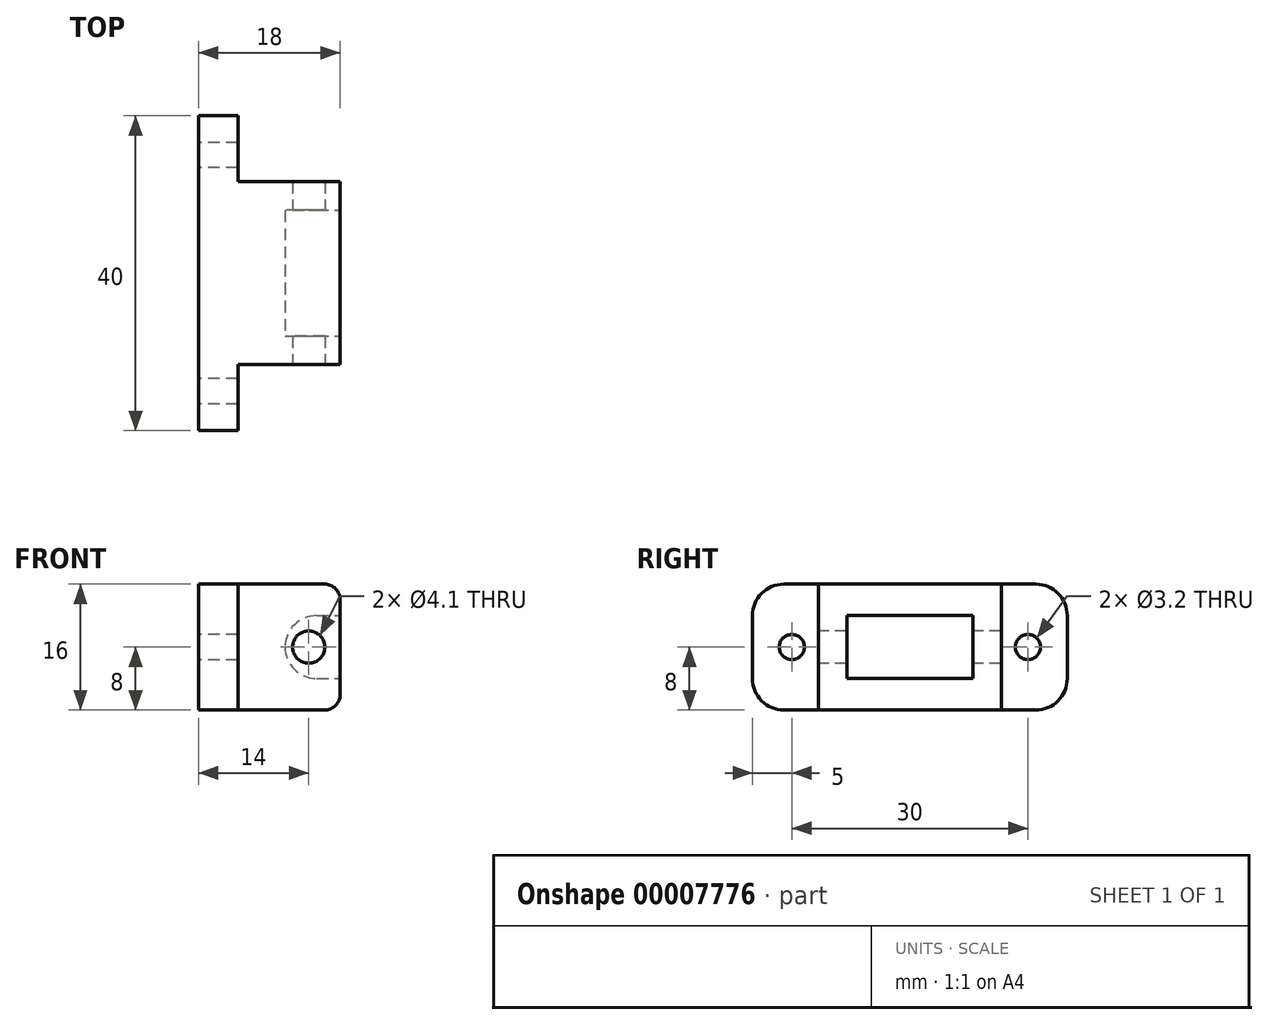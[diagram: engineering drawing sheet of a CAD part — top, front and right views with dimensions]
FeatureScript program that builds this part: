
annotation { "Feature Type Name" : "Feature", "Feature Type Description" : "" }
export const myFeature = defineFeature(function(context is Context, id is Id, definition is map)
    precondition{}
    {
        {
            var Q0;
            Q0=qCreatedBy(makeId("Right.planeOp"),FACE);
            var sketch = newSketch(context, id + "F0", { "sketchPlane" : qUnion([Q0])});
            skLineSegment(sketch, "E0.rect.bottom", {"start": v(16, 8) * mm, "end": v(-16, 8) * mm});
            skLineSegment(sketch, "E0.rect.top", {"start": v(16, -8) * mm, "end": v(-16, -8) * mm});
            skLineSegment(sketch, "E0.rect.left", {"start": v(20, 4) * mm, "end": v(20, -4) * mm});
            skLineSegment(sketch, "E0.rect.right", {"start": v(-20, 4) * mm, "end": v(-20, -4) * mm});
            skPoint(sketch, "E0.rect.middle", {"position": v(0, 0) * mm});
            skLineSegment(sketch, "E1", {"start": v(0, 11.54) * mm, "end": v(0, -21.77) * mm, "construction": true});
            skCircle(sketch, "E2", {"center": v(-15, 0) * mm, "radius": 1.6 * mm});
            skCircle(sketch, "E3.0.MirrorC", {"center": v(15, 0) * mm, "radius": 1.6 * mm});
            skPoint(sketch, "E4.visualSharp", {"position": v(-20, 8) * mm});
            skArc(sketch, "E4.filletArc", {"start": v(-16, 8) * mm, "mid": v(-18.83, 6.83) * mm, "end": v(-20, 4) * mm});
            skPoint(sketch, "E5.visualSharp", {"position": v(20, 8) * mm});
            skArc(sketch, "E5.filletArc", {"start": v(20, 4) * mm, "mid": v(18.83, 6.83) * mm, "end": v(16, 8) * mm});
            skPoint(sketch, "E6.visualSharp", {"position": v(20, -8) * mm});
            skArc(sketch, "E6.filletArc", {"start": v(16, -8) * mm, "mid": v(18.83, -6.83) * mm, "end": v(20, -4) * mm});
            skPoint(sketch, "E7.visualSharp", {"position": v(-20, -8) * mm});
            skArc(sketch, "E7.filletArc", {"start": v(-20, -4) * mm, "mid": v(-18.83, -6.83) * mm, "end": v(-16, -8) * mm});
            skSolve(sketch);
        }
        {
            var Q0;
            Q0 = qSketchRegion(id + "F0", true);
            extrude(context, id + "F1", {"entities" : qUnion([Q0]), "depth" : 10 * mm});
        }
        {
            var Q0;
            Q0=makeQuery(id+"F1.opExtrude","CAP_FACE",FACE,{"disambiguationData":[OSD([sQuery(id+"F0.wireOp",EDGE,"E0.rect.bottom"),sQuery(id+"F0.wireOp",EDGE,"E0.rect.top"),sQuery(id+"F0.wireOp",EDGE,"E0.rect.left"),sQuery(id+"F0.wireOp",EDGE,"E0.rect.right"),sQuery(id+"F0.wireOp",EDGE,"E2"),sQuery(id+"F0.wireOp",EDGE,"E3.0.MirrorC"),sQuery(id+"F0.wireOp",EDGE,"E4.filletArc"),sQuery(id+"F0.wireOp",EDGE,"E5.filletArc"),sQuery(id+"F0.wireOp",EDGE,"E6.filletArc"),sQuery(id+"F0.wireOp",EDGE,"E7.filletArc")])],"isStart":false});
            var sketch = newSketch(context, id + "F2", { "sketchPlane" : qUnion([Q0])});
            skLineSegment(sketch, "E8.rect.bottom", {"start": v(11.63, 8) * mm, "end": v(-11.63, 8) * mm});
            skLineSegment(sketch, "E8.rect.top", {"start": v(11.63, -8) * mm, "end": v(-11.63, -8) * mm});
            skLineSegment(sketch, "E8.rect.left", {"start": v(11.63, 8) * mm, "end": v(11.63, -8) * mm});
            skLineSegment(sketch, "E8.rect.right", {"start": v(-11.63, 8) * mm, "end": v(-11.63, -8) * mm});
            skPoint(sketch, "E8.rect.middle", {"position": v(0, 0) * mm});
            skSolve(sketch);
        }
        {
            var Q0;
            Q0 = qSketchRegion(id + "F2", true);
            extrude(context, id + "F3", {"entities" : qUnion([Q0]), "operationType" : NewBodyOperationType.ADD, "depth" : 8 * mm});
        }
        {
            var Q0;
            Q0=makeQuery(id+"F3.opExtrude","CAP_FACE",FACE,{"disambiguationData":[OSD([sQuery(id+"F2.wireOp",EDGE,"E8.rect.bottom"),sQuery(id+"F2.wireOp",EDGE,"E8.rect.top"),sQuery(id+"F2.wireOp",EDGE,"E8.rect.left"),sQuery(id+"F2.wireOp",EDGE,"E8.rect.right")])],"isStart":false});
            var sketch = newSketch(context, id + "F4", { "sketchPlane" : qUnion([Q0])});
            skLineSegment(sketch, "E9.rect.bottom", {"start": v(8, 4) * mm, "end": v(-8, 4) * mm});
            skLineSegment(sketch, "E9.rect.top", {"start": v(8, -4) * mm, "end": v(-8, -4) * mm});
            skLineSegment(sketch, "E9.rect.left", {"start": v(8, 4) * mm, "end": v(8, -4) * mm});
            skLineSegment(sketch, "E9.rect.right", {"start": v(-8, 4) * mm, "end": v(-8, -4) * mm});
            skPoint(sketch, "E9.rect.middle", {"position": v(0, 0) * mm});
            skSolve(sketch);
        }
        {
            var Q0;
            Q0 = qSketchRegion(id + "F4", true);
            extrude(context, id + "F5", {"entities" : qUnion([Q0]), "operationType" : NewBodyOperationType.REMOVE, "oppositeDirection" : true, "depth" : 7 * mm});
        }
        {
            var Q0;
            Q0=makeQuery(id+"F5.boolean.opBoolean","COPY",EDGE,{"derivedFrom":makeQuery(id+"F5.opExtrude","CAP_EDGE",EDGE,{"disambiguationData":[OSD([sQuery(id+"F4.wireOp",EDGE,"E9.rect.bottom")])],"isStart":false})});
            fillet(context, id + "F6", {"entities" : qUnion([Q0]), "radius" : 4 * mm, "tangentPropagation" : true, "allowEdgeOverflow" : false});
        }
        {
            var Q0;
            Q0=makeQuery(id+"F5.boolean.opBoolean","COPY",EDGE,{"derivedFrom":makeQuery(id+"F5.opExtrude","CAP_EDGE",EDGE,{"disambiguationData":[OSD([sQuery(id+"F4.wireOp",EDGE,"E9.rect.top")])],"isStart":false})});
            fillet(context, id + "F7", {"entities" : qUnion([Q0]), "radius" : 4 * mm, "tangentPropagation" : true, "allowEdgeOverflow" : false});
        }
        {
            var Q0;
            Q0=makeQuery(id+"F3.opExtrude","SWEPT_FACE",FACE,{"disambiguationData":[OSD([sQuery(id+"F2.wireOp",EDGE,"E8.rect.right")])]});
            var sketch = newSketch(context, id + "F8", { "sketchPlane" : qUnion([Q0])});
            skLineSegment(sketch, "E10", {"start": v(14, 8) * mm, "end": v(14, -8) * mm, "construction": true});
            skLineSegment(sketch, "E11", {"start": v(14, -8) * mm, "end": v(18, 0) * mm, "construction": true});
            skLineSegment(sketch, "E12", {"start": v(18, 0) * mm, "end": v(14, 0) * mm, "construction": true});
            skCircle(sketch, "E13", {"center": v(14, 0) * mm, "radius": 2.05 * mm});
            skSolve(sketch);
        }
        {
            var Q0;
            Q0 = qSketchRegion(id + "F8", true);
            extrude(context, id + "F9", {"entities" : qUnion([Q0]), "operationType" : NewBodyOperationType.REMOVE, "endBound" : BoundingType.THROUGH_ALL, "oppositeDirection" : true, "depth" : 25 * mm});
        }
        {
            var Q0;
            Q0=makeQuery(id+"F3.opExtrude","CAP_EDGE",EDGE,{"disambiguationData":[OSD([sQuery(id+"F2.wireOp",EDGE,"E8.rect.bottom")])],"isStart":false});
            var Q1;
            Q1=makeQuery(id+"F3.opExtrude","CAP_EDGE",EDGE,{"disambiguationData":[OSD([sQuery(id+"F2.wireOp",EDGE,"E8.rect.top")])],"isStart":false});
            var Q2;
            Q2=makeQuery(id+"F5.boolean.opBoolean","COPY",EDGE,{"derivedFrom":makeQuery(id+"F5.opExtrude","CAP_EDGE",EDGE,{"disambiguationData":[OSD([sQuery(id+"F4.wireOp",EDGE,"E9.rect.top")])],"isStart":true})});
            var Q3;
            Q3=makeQuery(id+"F5.boolean.opBoolean","COPY",EDGE,{"derivedFrom":makeQuery(id+"F5.opExtrude","CAP_EDGE",EDGE,{"disambiguationData":[OSD([sQuery(id+"F4.wireOp",EDGE,"E9.rect.bottom")])],"isStart":true})});
            fillet(context, id + "F10", {"entities" : qUnion([Q0, Q1, Q2, Q3]), "radius" : 2 * mm, "tangentPropagation" : true, "allowEdgeOverflow" : false});
        }
        {
            var Q0;
            {var subQ0=sQuery(id+"F0.wireOp",EDGE,"E0.rect.bottom");var subQ1=sQuery(id+"F0.wireOp",EDGE,"E0.rect.top");var subQ2=sQuery(id+"F0.wireOp",EDGE,"E0.rect.right");var subQ3=sQuery(id+"F0.wireOp",EDGE,"E2");var subQ4=sQuery(id+"F0.wireOp",EDGE,"E4.filletArc");var subQ5=sQuery(id+"F0.wireOp",EDGE,"E7.filletArc");Q0=makeQuery(id+"F3.boolean.opBoolean","SPLIT",FACE,{"disambiguationData":[TD([makeQuery(id+"F1.opExtrude","SWEPT_FACE",FACE,{"disambiguationData":[OSD([subQ2])]})])],"derivedFrom":makeQuery(id+"F1.opExtrude","CAP_FACE",FACE,{"disambiguationData":[OSD([subQ0,subQ1,sQuery(id+"F0.wireOp",EDGE,"E0.rect.left"),subQ2,subQ3,sQuery(id+"F0.wireOp",EDGE,"E3.0.MirrorC"),subQ4,sQuery(id+"F0.wireOp",EDGE,"E5.filletArc"),sQuery(id+"F0.wireOp",EDGE,"E6.filletArc"),subQ5])],"isStart":false})});}
            var Q1;
            {var subQ0=sQuery(id+"F0.wireOp",EDGE,"E0.rect.bottom");var subQ1=sQuery(id+"F0.wireOp",EDGE,"E0.rect.top");var subQ2=sQuery(id+"F0.wireOp",EDGE,"E0.rect.left");var subQ3=sQuery(id+"F0.wireOp",EDGE,"E3.0.MirrorC");var subQ4=sQuery(id+"F0.wireOp",EDGE,"E5.filletArc");var subQ5=sQuery(id+"F0.wireOp",EDGE,"E6.filletArc");Q1=makeQuery(id+"F3.boolean.opBoolean","SPLIT",FACE,{"disambiguationData":[TD([makeQuery(id+"F1.opExtrude","SWEPT_FACE",FACE,{"disambiguationData":[OSD([subQ2])]})])],"derivedFrom":makeQuery(id+"F1.opExtrude","CAP_FACE",FACE,{"disambiguationData":[OSD([subQ0,subQ1,subQ2,sQuery(id+"F0.wireOp",EDGE,"E0.rect.right"),sQuery(id+"F0.wireOp",EDGE,"E2"),subQ3,sQuery(id+"F0.wireOp",EDGE,"E4.filletArc"),subQ4,subQ5,sQuery(id+"F0.wireOp",EDGE,"E7.filletArc")])],"isStart":false})});}
            extrude(context, id + "F11", {"entities" : qUnion([Q0, Q1]), "operationType" : NewBodyOperationType.REMOVE, "oppositeDirection" : true, "depth" : 5 * mm});
        }
    });
